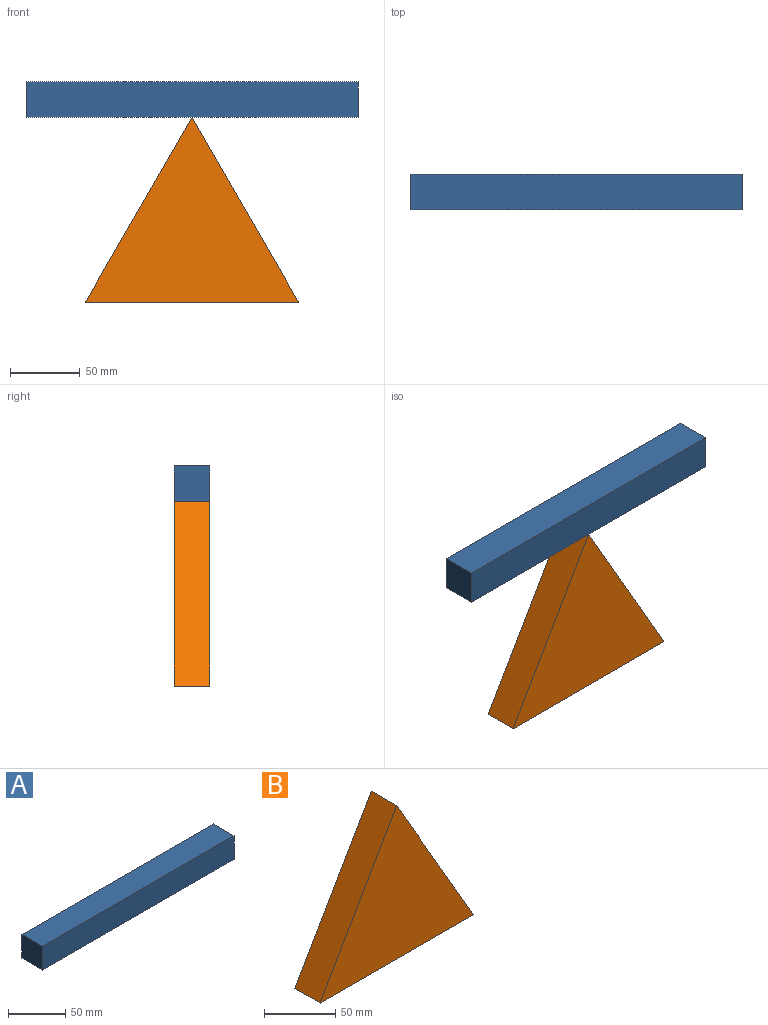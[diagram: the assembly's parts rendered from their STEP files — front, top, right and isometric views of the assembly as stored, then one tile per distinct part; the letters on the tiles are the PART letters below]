
ASSEMBLY  parts=2 mates=1
PART A: 6 faces, bbox 237.2x25.4x25.3 mm
  f0: plane 237.24x25.4mm, normal (0,0,1), area 6026mm2, adj f1,f3,f4,f5
  f1: plane 25.4x25.34mm, normal (-1,0,0), area 643.6mm2, adj f0,f2,f4,f5
  f2: plane 237.24x25.4mm, normal (0,0,-1), area 6026mm2, adj f1,f3,f4,f5
  f3: plane 25.4x25.34mm, normal (1,0,0), area 643.6mm2, adj f0,f2,f4,f5
  f4: plane 237.24x25.34mm, normal (0,-1,0), area 6011.8mm2, adj f0,f1,f2,f3
  f5: plane 237.24x25.34mm, normal (0,1,0), area 6011.8mm2, adj f0,f1,f2,f3
PART B: 5 faces, bbox 152.4x25.4x132 mm
  f0: plane 131.98x76.2mm, normal (0.87,0,0.5), area 3871mm2, adj f1,f2,f3,f4
  f1: plane 131.98x76.2mm, normal (-0.87,0,0.5), area 3871mm2, adj f0,f2,f3,f4
  f2: plane 152.4x25.4mm, normal (0,0,-1), area 3871mm2, adj f0,f1,f3,f4
  f3: plane 152.4x131.98mm, normal (0,-1,0), area 10057mm2, adj f0,f1,f2
  f4: plane 152.4x131.98mm, normal (0,1,0), area 10057mm2, adj f0,f1,f2
PLACE A rot(axis=(0,1,0),0deg) t=(55.04,87.55,103.45)mm
PLACE B t=(67.03,87.55,-28.53)mm
MATE revolute A.f4 <-> B.f3  axis (0,-1,0) through (67.03,62.15,103.45)mm
